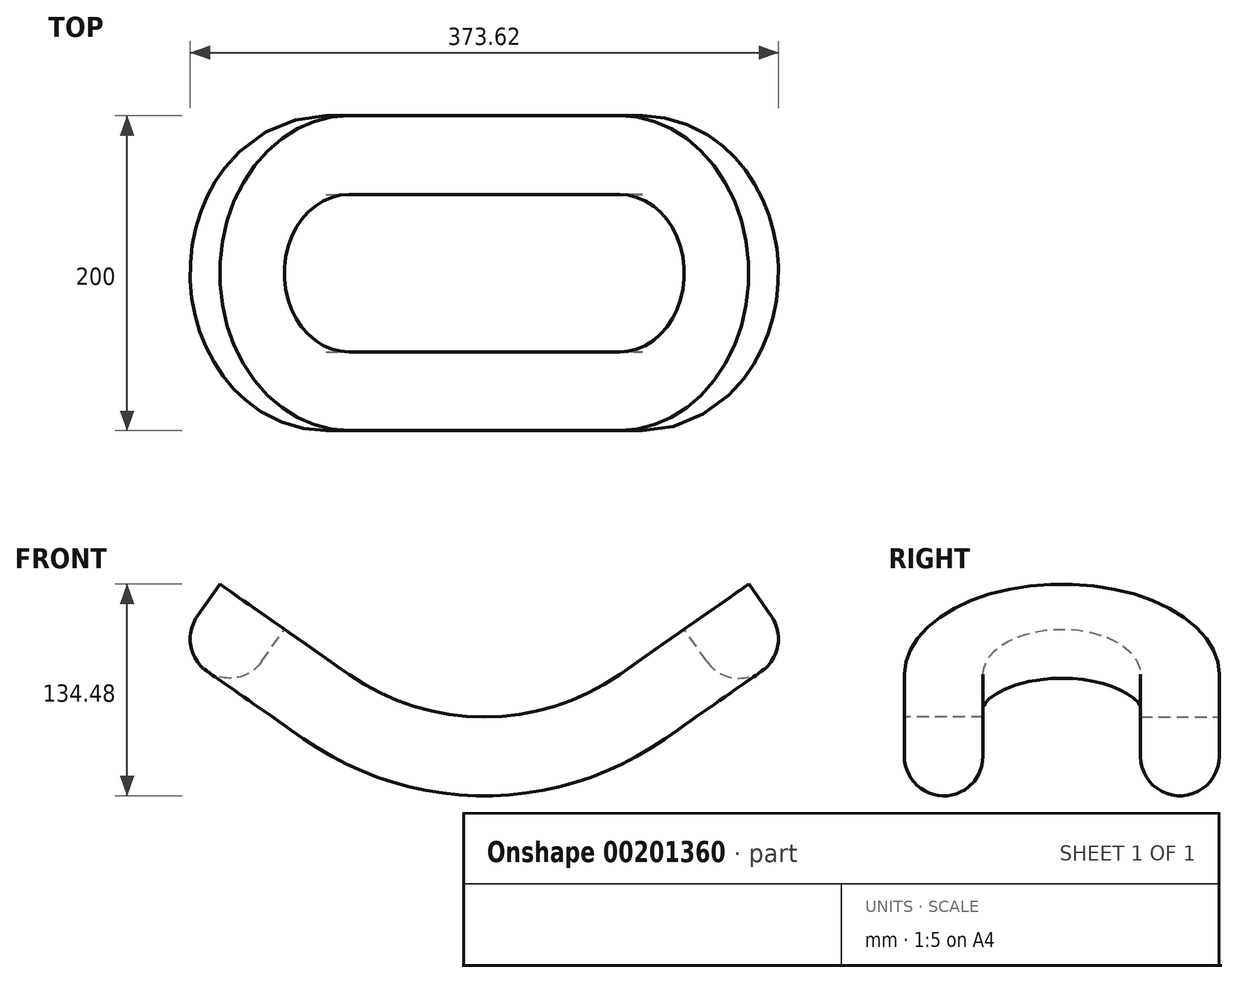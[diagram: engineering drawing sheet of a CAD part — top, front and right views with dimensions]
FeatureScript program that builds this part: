
annotation { "Feature Type Name" : "Feature", "Feature Type Description" : "" }
export const myFeature = defineFeature(function(context is Context, id is Id, definition is map)
    precondition{}
    {
        {
            var Q0;
            Q0=qCreatedBy(makeId("Front.planeOp"),FACE);
            var sketch = newSketch(context, id + "F0", { "sketchPlane" : qUnion([Q0])});
            skArc(sketch, "E0", {"start": v(0, 0) * mm, "mid": v(60.14, 9.26) * mm, "end": v(114.72, 36.17) * mm});
            skLineSegment(sketch, "E1", {"start": v(114.72, 36.17) * mm, "end": v(176.15, 79.19) * mm});
            skLineSegment(sketch, "E2", {"start": v(0, 200) * mm, "end": v(114.72, 36.17) * mm, "construction": true});
            skSolve(sketch);
        }
        {
            var Q0;
            Q0 = qSketchRegion(id + "F0", true);
            var Q1;
            Q1 = qConstructionFilter(qBodyType(qCreatedBy(id + "F0" ,EDGE), BodyType.WIRE), ConstructionObject.NO);
            extrude(context, id + "F1", {"entities" : qUnion([Q0]), "bodyType" : ToolBodyType.SURFACE, "operationType" : NewBodyOperationType.INTERSECT, "surfaceEntities" : qUnion([Q1]), "depth" : 75 * mm});
        }
        {
            var Q0;
            Q0=makeQuery(id+"F1.opExtrude","SWEPT_FACE",FACE,{"disambiguationData":[OSD([sQuery(id+"F0.wireOp",EDGE,"E1")])]});
            var sketch = newSketch(context, id + "F2", { "sketchPlane" : qUnion([Q0])});
            skArc(sketch, "E3", {"start": v(114.72, 75) * mm, "mid": v(167.75, 53.03) * mm, "end": v(189.72, 0) * mm});
            skSolve(sketch);
        }
        {
            var Q0;
            Q0=qCreatedBy(makeId("Right.planeOp"),FACE);
            var sketch = newSketch(context, id + "F3", { "sketchPlane" : qUnion([Q0])});
            skLineSegment(sketch, "E4.top", {"start": v(-100, 50) * mm, "end": v(-50, 50) * mm});
            skLineSegment(sketch, "E4.left", {"start": v(-100, 25) * mm, "end": v(-100, 50) * mm});
            skLineSegment(sketch, "E4.right", {"start": v(-50, 25) * mm, "end": v(-50, 50) * mm});
            skPoint(sketch, "E4.middle", {"position": v(-75, 37.5) * mm});
            skArc(sketch, "E5", {"start": v(-50, 25) * mm, "mid": v(-75, 0) * mm, "end": v(-100, 25) * mm});
            skSolve(sketch);
        }
        {
            var Q0;
            Q0=makeQuery(id+"F3.imprint","IMPRINT",FACE,{"disambiguationData":[TD([[makeQuery(id+"F3.imprint","IMPRINT",EDGE,{"derivedFrom":sQuery(id+"F3.wireOp",EDGE,"E4.top")}),-1.0]])]});
            var Q1;
            Q1=makeQuery(id+"F1.opExtrude","CAP_EDGE",EDGE,{"disambiguationData":[OSD([sQuery(id+"F0.wireOp",EDGE,"E0")])],"isStart":false});
            var Q2;
            Q2=sQuery(id+"F2.wireOp",EDGE,"E3");
            sweep(context, id + "F4", {"profiles" : qUnion([Q0]), "path" : qUnion([Q1, Q2])});
        }
        {
            var Q0;
            Q0=makeQuery(id+"F4.opSweep","SWEPT_BODY",BODY,{"disambiguationData":[OSD([sQuery(id+"F2.wireOp",EDGE,"E3"),sQuery(id+"F3.wireOp",EDGE,"E4.top"),sQuery(id+"F3.wireOp",EDGE,"E4.left"),sQuery(id+"F3.wireOp",EDGE,"E4.right"),sQuery(id+"F3.wireOp",EDGE,"E5")])]});
            var Q1;
            Q1=qCreatedBy(makeId("Front.planeOp"),FACE);
            mirror(context, id + "F5", {"operationType" : NewBodyOperationType.ADD, "entities" : qUnion([Q0]), "mirrorPlane" : qUnion([Q1])});
        }
        {
            var Q0;
            Q0=makeQuery(id+"F4.opSweep","SWEPT_BODY",BODY,{"disambiguationData":[OSD([sQuery(id+"F2.wireOp",EDGE,"E3"),sQuery(id+"F3.wireOp",EDGE,"E4.top"),sQuery(id+"F3.wireOp",EDGE,"E4.left"),sQuery(id+"F3.wireOp",EDGE,"E4.right"),sQuery(id+"F3.wireOp",EDGE,"E5")])]});
            var Q1;
            Q1=qCreatedBy(makeId("Right.planeOp"),FACE);
            mirror(context, id + "F6", {"operationType" : NewBodyOperationType.ADD, "entities" : qUnion([Q0]), "mirrorPlane" : qUnion([Q1])});
        }
    });
